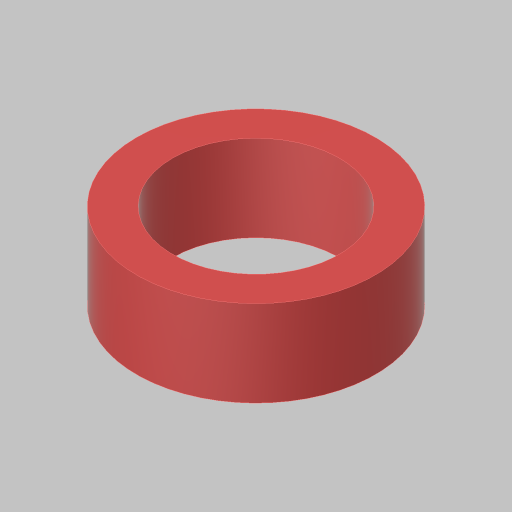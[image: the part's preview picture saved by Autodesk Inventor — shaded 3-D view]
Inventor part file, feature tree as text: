
AUTODESK INVENTOR PART (.ipt)
format: ipt  version: 2023.5 (Build 275446000, 446)  size: 100,864 bytes
history: native  units: in
note: dims shown in document units (in); Inventor stores cm internally (conversion verified against a paired STEP export)
features: extrude x1, sketch x1
ambient origin geometry x8: Origin, YZ Plane, XZ Plane, XY Plane, X Axis, Y Axis, Z Axis, Center Point
bodies: Solid1 (feature_tree)
feature tree (2):
  extrude  "Extrusion1"  Depth=0.3in
  sketch  "Sketch1"  dims[d0=0.58in d1=0.125in d2=0.3in d3=0.0in]
